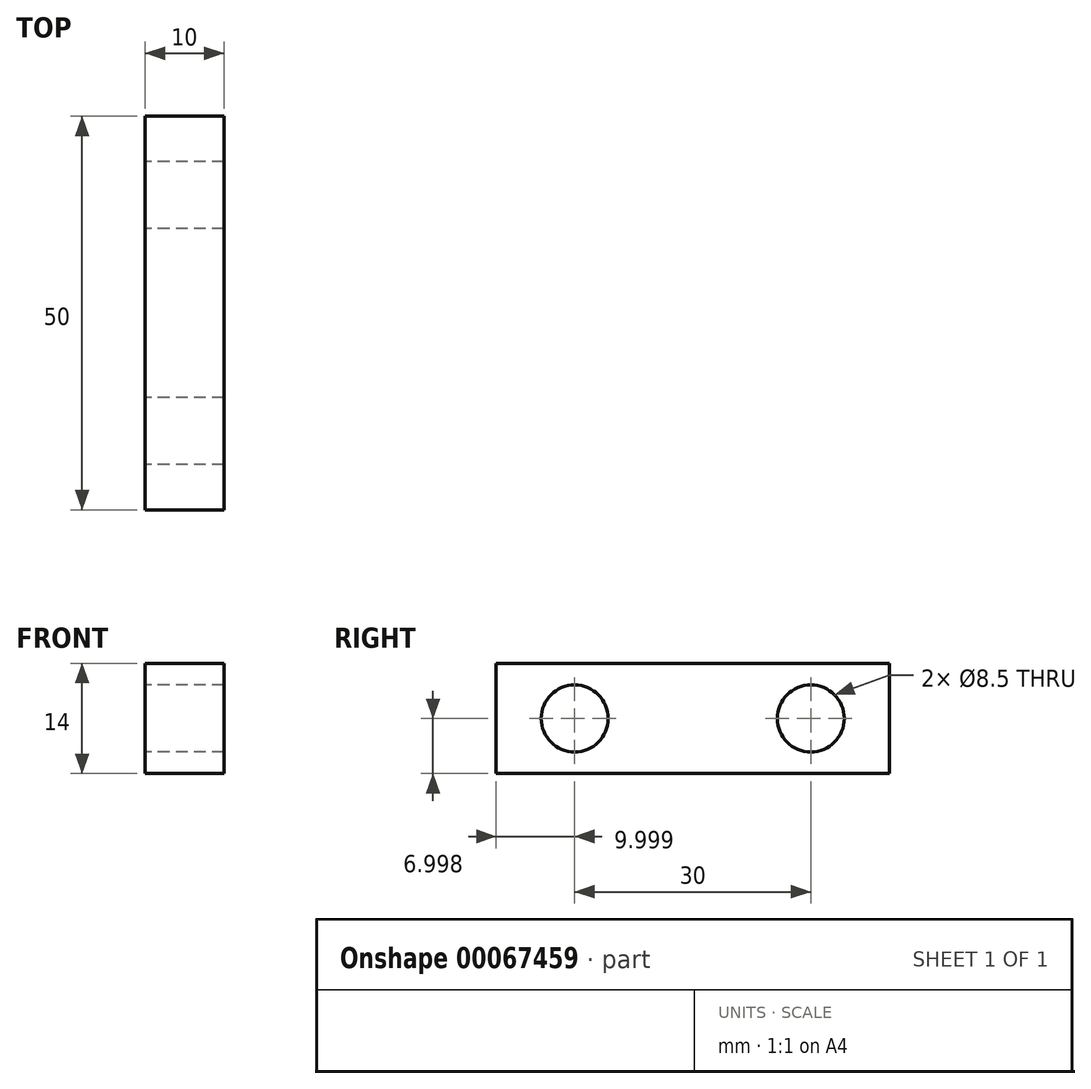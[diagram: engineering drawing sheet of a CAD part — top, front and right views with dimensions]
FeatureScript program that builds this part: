
annotation { "Feature Type Name" : "Feature", "Feature Type Description" : "" }
export const myFeature = defineFeature(function(context is Context, id is Id, definition is map)
    precondition{}
    {
        {
            var Q0;
            Q0=qCreatedBy(makeId("Right.planeOp"),FACE);
            var sketch = newSketch(context, id + "F0", { "sketchPlane" : qUnion([Q0])});
            skLineSegment(sketch, "E0.bottom", {"start": v(-50.7, 7.17) * mm, "end": v(-0.7, 7.17) * mm});
            skLineSegment(sketch, "E0.top", {"start": v(-50.7, 21.17) * mm, "end": v(-0.7, 21.17) * mm});
            skLineSegment(sketch, "E0.left", {"start": v(-50.7, 7.17) * mm, "end": v(-50.7, 21.17) * mm});
            skLineSegment(sketch, "E1", {"start": v(-0.7, 21.17) * mm, "end": v(-0.7, 7.17) * mm});
            skPoint(sketch, "E2", {"position": v(-40.7, 14.17) * mm});
            skPoint(sketch, "E3", {"position": v(-10.7, 14.17) * mm});
            skSolve(sketch);
        }
        {
            var Q0;
            Q0 = qSketchRegion(id + "F0", true);
            extrude(context, id + "F1", {"entities" : qUnion([Q0]), "depth" : 10 * mm});
        }
        {
            var Q0;
            Q0=sQuery(id+"F0.wireOp",VERTEX,"E2");
            var Q1;
            Q1=sQuery(id+"F0.wireOp",VERTEX,"E3");
            var Q2;
            Q2=makeQuery(id+"F1.opExtrude","SWEPT_BODY",BODY,{"disambiguationData":[OSD([sQuery(id+"F0.wireOp",EDGE,"E0.bottom"),sQuery(id+"F0.wireOp",EDGE,"E0.top"),sQuery(id+"F0.wireOp",EDGE,"E0.left"),sQuery(id+"F0.wireOp",EDGE,"E1")])]});
            hole(context, id + "F2", {"style" : HoleStyle.SIMPLE, "holeDiameter" : 8.5 * mm, "endStyle" : HoleEndStyle.THROUGH, "oppositeDirection" : true, "locations" : qUnion([Q0, Q1]), "scope" : qUnion([Q2])});
        }
    });
